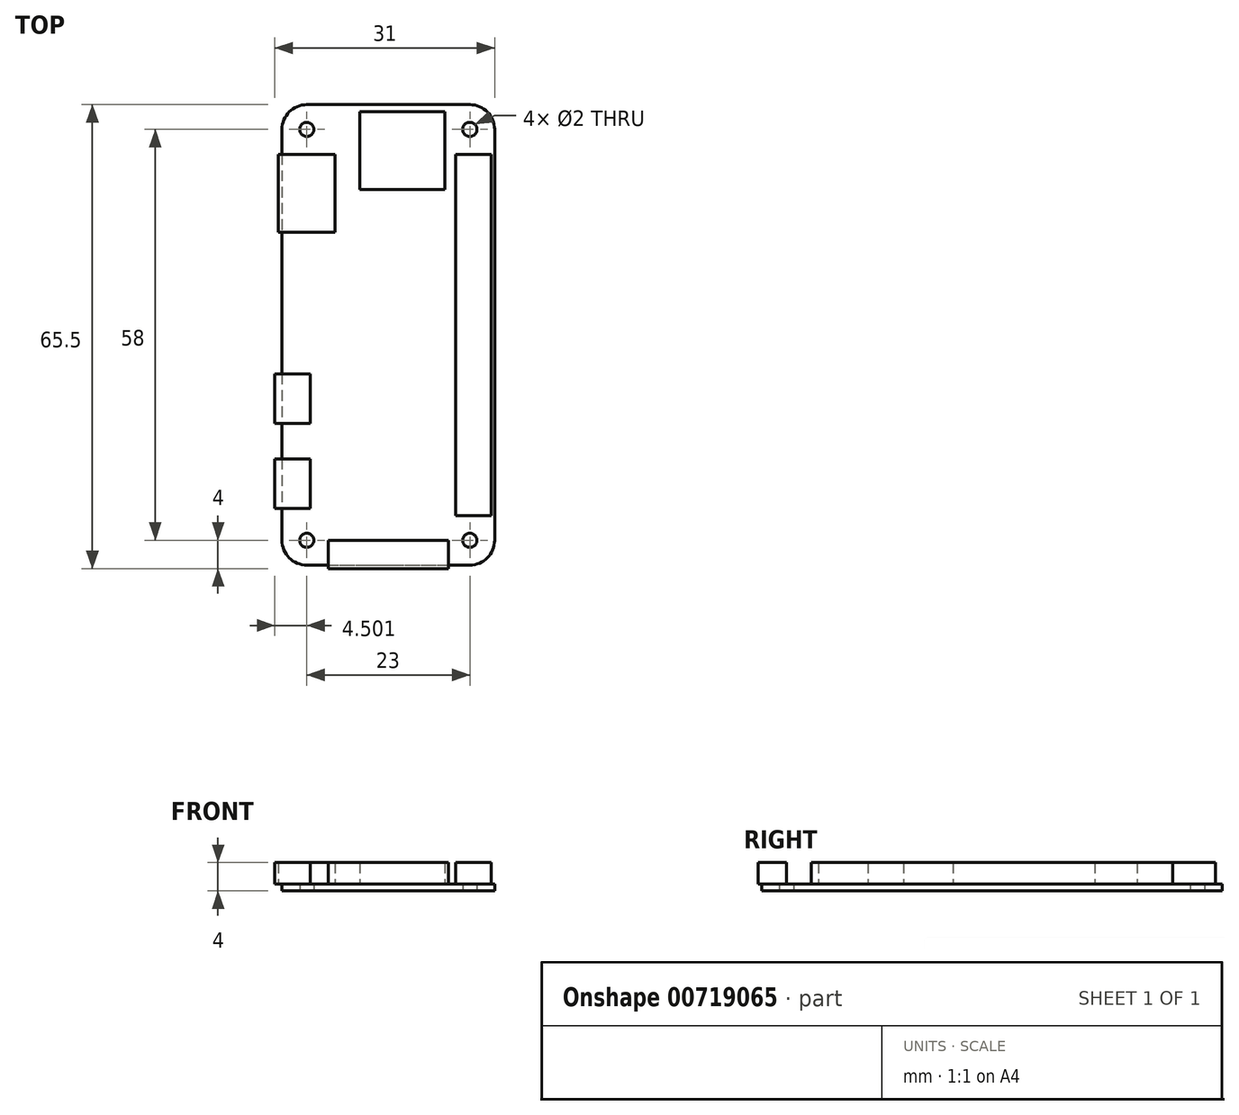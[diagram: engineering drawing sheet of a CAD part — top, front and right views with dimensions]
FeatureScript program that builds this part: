
annotation { "Feature Type Name" : "Feature", "Feature Type Description" : "" }
export const myFeature = defineFeature(function(context is Context, id is Id, definition is map)
    precondition{}
    {
        {
            var Q0;
            Q0=qCreatedBy(makeId("Top.planeOp"),FACE);
            var sketch = newSketch(context, id + "F0", { "sketchPlane" : qUnion([Q0])});
            skLineSegment(sketch, "E0.bottom", {"start": v(-9.88, 32.1) * mm, "end": v(13.12, 32.1) * mm});
            skLineSegment(sketch, "E0.top", {"start": v(-9.88, -32.9) * mm, "end": v(13.12, -32.9) * mm});
            skLineSegment(sketch, "E0.left", {"start": v(-13.38, 28.6) * mm, "end": v(-13.38, -29.4) * mm});
            skLineSegment(sketch, "E0.right", {"start": v(16.62, 28.6) * mm, "end": v(16.62, -29.4) * mm});
            skPoint(sketch, "E1.visualSharp", {"position": v(16.62, 32.1) * mm});
            skArc(sketch, "E1.filletArc", {"start": v(16.62, 28.6) * mm, "mid": v(15.6, 31.08) * mm, "end": v(13.12, 32.1) * mm});
            skPoint(sketch, "E2.visualSharp", {"position": v(-13.38, 32.1) * mm});
            skArc(sketch, "E2.filletArc", {"start": v(-9.88, 32.1) * mm, "mid": v(-12.35, 31.08) * mm, "end": v(-13.38, 28.6) * mm});
            skPoint(sketch, "E3.visualSharp", {"position": v(16.62, -32.9) * mm});
            skArc(sketch, "E3.filletArc", {"start": v(13.12, -32.9) * mm, "mid": v(15.6, -31.87) * mm, "end": v(16.62, -29.4) * mm});
            skPoint(sketch, "E4.visualSharp", {"position": v(-13.38, -32.9) * mm});
            skArc(sketch, "E4.filletArc", {"start": v(-13.38, -29.4) * mm, "mid": v(-12.35, -31.87) * mm, "end": v(-9.88, -32.9) * mm});
            skCircle(sketch, "E5", {"center": v(13.12, -29.4) * mm, "radius": 1 * mm});
            skCircle(sketch, "E6", {"center": v(-9.88, -29.4) * mm, "radius": 1 * mm});
            skCircle(sketch, "E7", {"center": v(-9.88, 28.6) * mm, "radius": 1 * mm});
            skCircle(sketch, "E8", {"center": v(13.12, 28.6) * mm, "radius": 1 * mm});
            skSolve(sketch);
        }
        {
            var Q0;
            Q0=makeQuery(id+"F0.imprint","IMPRINT",FACE,{"disambiguationData":[TD([[makeQuery(id+"F0.imprint","IMPRINT",EDGE,{"derivedFrom":sQuery(id+"F0.wireOp",EDGE,"E0.bottom")}),-1.0]])]});
            extrude(context, id + "F1", {"entities" : qUnion([Q0]), "depth" : 1 * mm, "offsetDistance" : 25 * mm});
        }
        {
            var Q0;
            Q0=makeQuery(id+"F1.opExtrude","CAP_FACE",FACE,{"disambiguationData":[OSD([sQuery(id+"F0.wireOp",EDGE,"E0.bottom"),sQuery(id+"F0.wireOp",EDGE,"E0.top"),sQuery(id+"F0.wireOp",EDGE,"E0.left"),sQuery(id+"F0.wireOp",EDGE,"E0.right"),sQuery(id+"F0.wireOp",EDGE,"E1.filletArc"),sQuery(id+"F0.wireOp",EDGE,"E2.filletArc"),sQuery(id+"F0.wireOp",EDGE,"E3.filletArc"),sQuery(id+"F0.wireOp",EDGE,"E4.filletArc"),sQuery(id+"F0.wireOp",EDGE,"E5"),sQuery(id+"F0.wireOp",EDGE,"E6"),sQuery(id+"F0.wireOp",EDGE,"E7"),sQuery(id+"F0.wireOp",EDGE,"E8")])],"isStart":false});
            var sketch = newSketch(context, id + "F2", { "sketchPlane" : qUnion([Q0])});
            skLineSegment(sketch, "E9.bottom", {"start": v(-2.38, 31.1) * mm, "end": v(9.62, 31.1) * mm});
            skLineSegment(sketch, "E9.top", {"start": v(-2.38, 20.1) * mm, "end": v(9.62, 20.1) * mm});
            skLineSegment(sketch, "E9.left", {"start": v(-2.38, 31.1) * mm, "end": v(-2.38, 20.1) * mm});
            skLineSegment(sketch, "E9.right", {"start": v(9.62, 31.1) * mm, "end": v(9.62, 20.1) * mm});
            skLineSegment(sketch, "E10.bottom", {"start": v(-13.88, 25.1) * mm, "end": v(-5.88, 25.1) * mm});
            skLineSegment(sketch, "E10.top", {"start": v(-13.88, 14.1) * mm, "end": v(-5.88, 14.1) * mm});
            skLineSegment(sketch, "E10.left", {"start": v(-13.88, 25.1) * mm, "end": v(-13.88, 14.1) * mm});
            skLineSegment(sketch, "E10.right", {"start": v(-5.88, 25.1) * mm, "end": v(-5.88, 14.1) * mm});
            skLineSegment(sketch, "E11.bottom", {"start": v(-14.38, -24.9) * mm, "end": v(-9.38, -24.9) * mm});
            skLineSegment(sketch, "E11.top", {"start": v(-14.38, -17.9) * mm, "end": v(-9.38, -17.9) * mm});
            skLineSegment(sketch, "E11.left", {"start": v(-14.38, -24.9) * mm, "end": v(-14.38, -17.9) * mm});
            skLineSegment(sketch, "E11.right", {"start": v(-9.38, -24.9) * mm, "end": v(-9.38, -17.9) * mm});
            skLineSegment(sketch, "E12.bottom", {"start": v(-14.38, -12.9) * mm, "end": v(-9.38, -12.9) * mm});
            skLineSegment(sketch, "E12.top", {"start": v(-14.38, -5.9) * mm, "end": v(-9.38, -5.9) * mm});
            skLineSegment(sketch, "E12.left", {"start": v(-14.38, -12.9) * mm, "end": v(-14.38, -5.9) * mm});
            skLineSegment(sketch, "E12.right", {"start": v(-9.38, -12.9) * mm, "end": v(-9.38, -5.9) * mm});
            skLineSegment(sketch, "E13.bottom", {"start": v(-6.88, -29.4) * mm, "end": v(10.12, -29.4) * mm});
            skLineSegment(sketch, "E13.top", {"start": v(-6.88, -33.4) * mm, "end": v(10.12, -33.4) * mm});
            skLineSegment(sketch, "E13.left", {"start": v(-6.88, -29.4) * mm, "end": v(-6.88, -33.4) * mm});
            skLineSegment(sketch, "E13.right", {"start": v(10.12, -29.4) * mm, "end": v(10.12, -33.4) * mm});
            skLineSegment(sketch, "E14.bottom", {"start": v(11.12, 25.1) * mm, "end": v(16.12, 25.1) * mm});
            skLineSegment(sketch, "E14.top", {"start": v(11.12, -25.9) * mm, "end": v(16.12, -25.9) * mm});
            skLineSegment(sketch, "E14.left", {"start": v(11.12, 25.1) * mm, "end": v(11.12, -25.9) * mm});
            skLineSegment(sketch, "E14.right", {"start": v(16.12, 25.1) * mm, "end": v(16.12, -25.9) * mm});
            skSolve(sketch);
        }
        {
            var Q0;
            Q0 = qSketchRegion(id + "F2", true);
            extrude(context, id + "F3", {"entities" : qUnion([Q0]), "operationType" : NewBodyOperationType.ADD, "depth" : 3 * mm, "offsetDistance" : 25 * mm});
        }
    });
